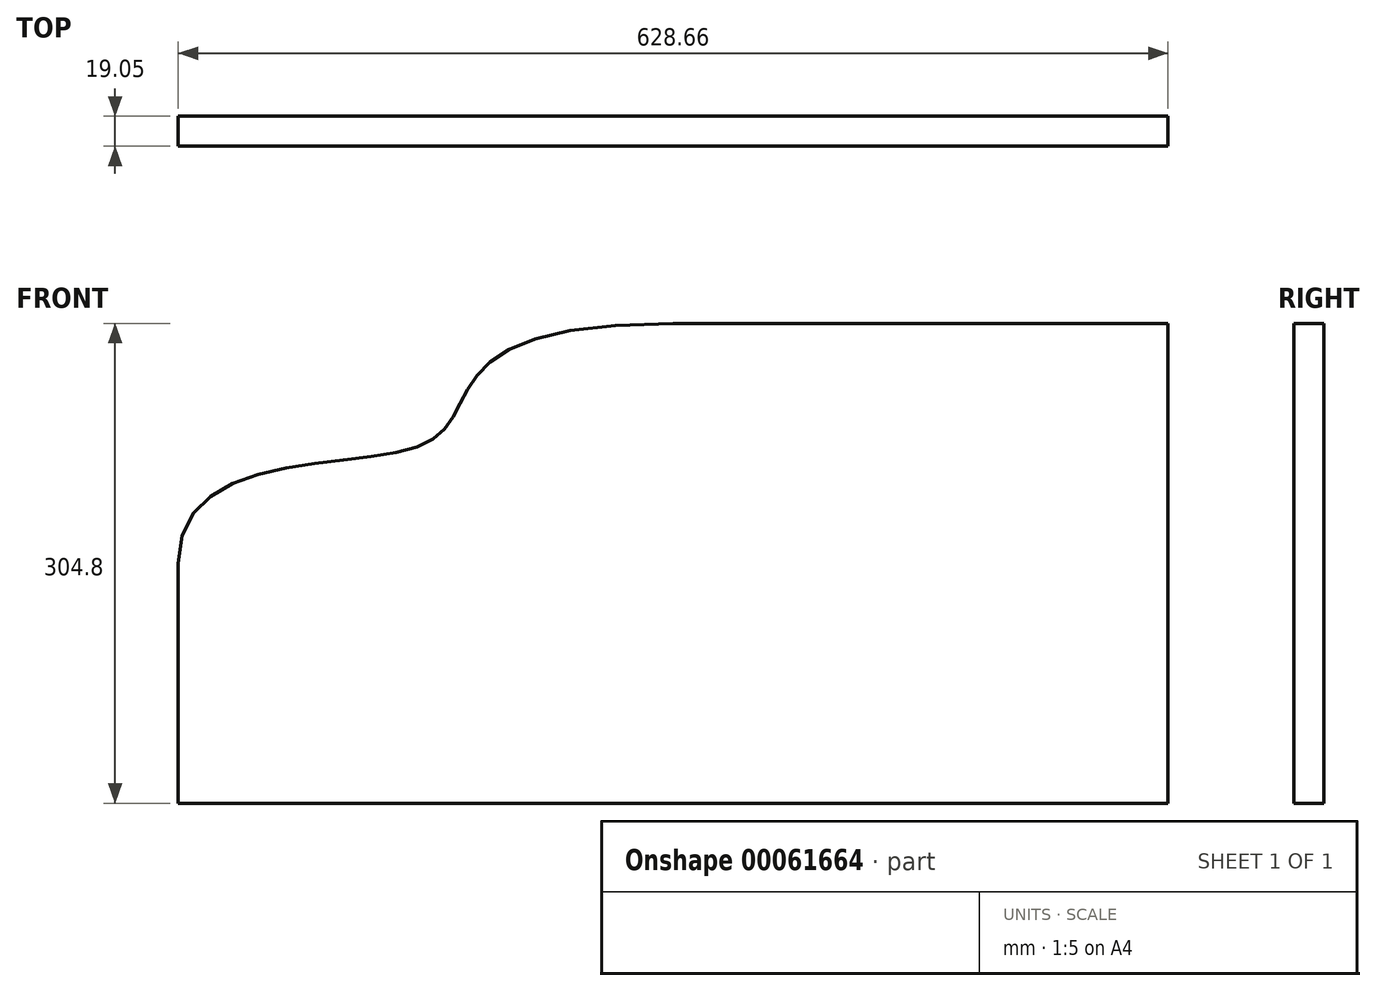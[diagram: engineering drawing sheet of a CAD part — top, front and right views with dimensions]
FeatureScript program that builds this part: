
annotation { "Feature Type Name" : "Feature", "Feature Type Description" : "" }
export const myFeature = defineFeature(function(context is Context, id is Id, definition is map)
    precondition{}
    {
        {
            var Q0;
            Q0=qCreatedBy(makeId("Front.planeOp"),FACE);
            var sketch = newSketch(context, id + "F0", { "sketchPlane" : qUnion([Q0])});
            skLineSegment(sketch, "E0", {"start": v(-417.36, 0) * mm, "end": v(417.36, 0) * mm, "construction": true});
            skLineSegment(sketch, "E1", {"start": v(0, 330.1) * mm, "end": v(0, -330.1) * mm, "construction": true});
            skLineSegment(sketch, "E2.bottom", {"start": v(-314.33, -152.4) * mm, "end": v(314.33, -152.4) * mm});
            skLineSegment(sketch, "E2.top", {"start": v(-314.33, 152.4) * mm, "end": v(314.33, 152.4) * mm});
            skLineSegment(sketch, "E2.left", {"start": v(-314.33, -152.4) * mm, "end": v(-314.33, 152.4) * mm});
            skLineSegment(sketch, "E2.right", {"start": v(314.33, -152.4) * mm, "end": v(314.33, 152.4) * mm});
            skLineSegment(sketch, "E3", {"start": v(-417.36, 76.2) * mm, "end": v(417.36, 76.2) * mm, "construction": true});
            skLineSegment(sketch, "E4", {"start": v(-417.36, 0) * mm, "end": v(-417.36, 76.2) * mm, "construction": true});
            skLineSegment(sketch, "E5", {"start": v(-314.33, 76.2) * mm, "end": v(0, 76.2) * mm, "construction": true});
            skFitSpline(sketch, "E6", {"points": [v(0, 152.4) * mm, v(-157.16, 76.2) * mm, v(-314.33, 0) * mm], "startDerivative": vector(-942.97, 0) * mm, "endDerivative": vector(0, -457.2) * mm});
            skLineSegment(sketch, "E7", {"start": v(-157.16, 76.2) * mm, "end": v(-157.16, 152.4) * mm, "construction": true});
            skSolve(sketch);
        }
        {
            var Q0;
            {var subQ2=sQuery(id+"F0.wireOp",EDGE,"E2.bottom");Q0=makeQuery(id+"F0.imprint","IMPRINT",FACE,{"disambiguationData":[TD([[makeQuery(id+"F0.imprint","IMPRINT",EDGE,{"derivedFrom":subQ2}),1.0]])]});}
            extrude(context, id + "F1", {"entities" : qUnion([Q0]), "depth" : 19.05 * mm});
        }
    });
